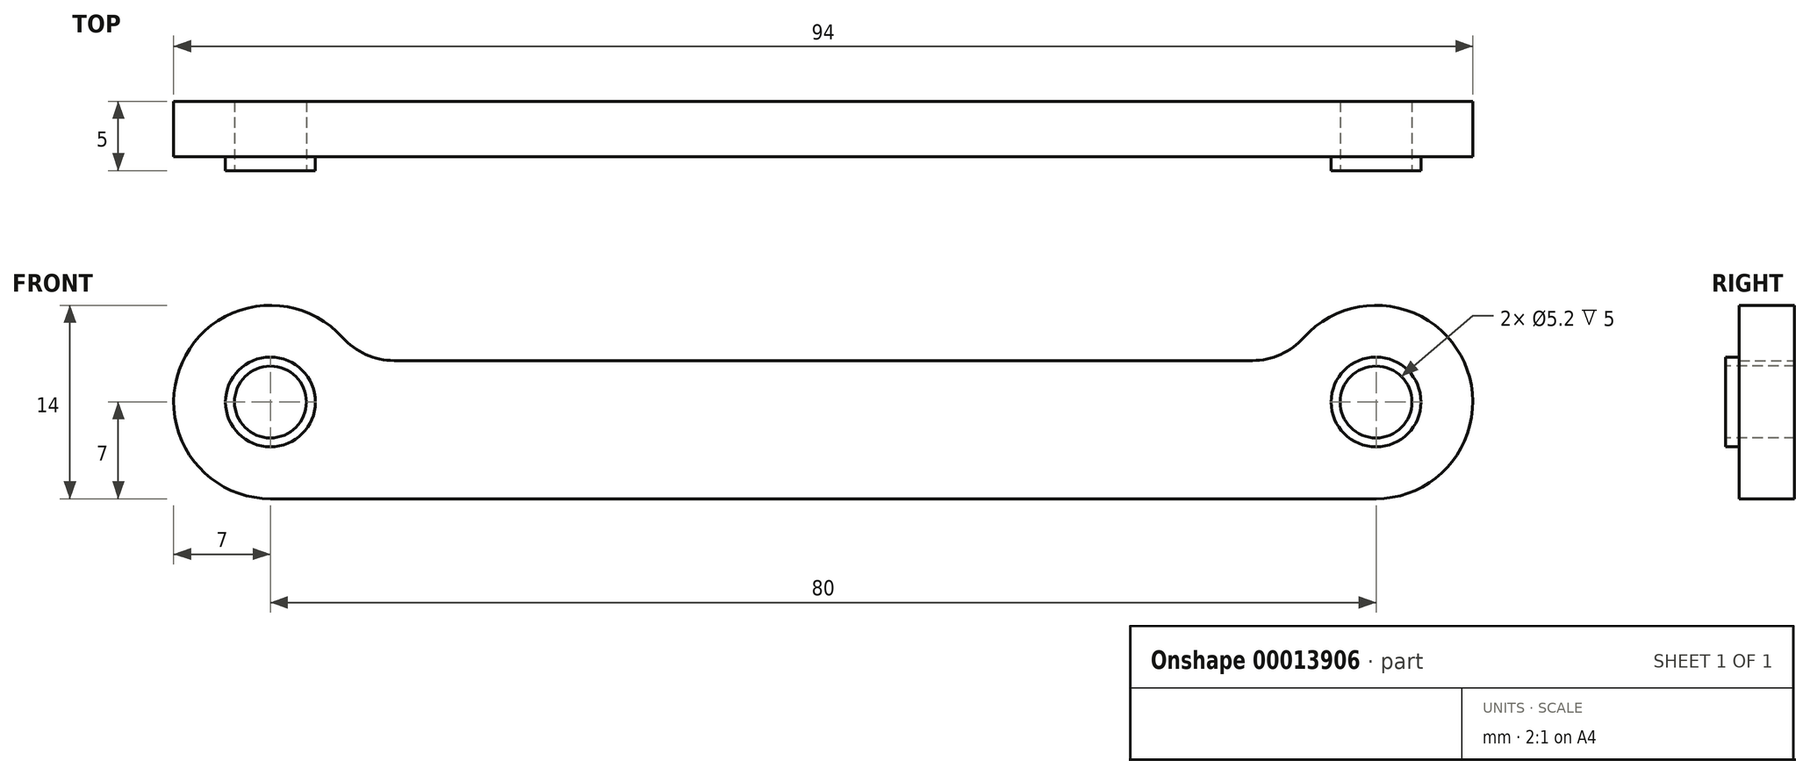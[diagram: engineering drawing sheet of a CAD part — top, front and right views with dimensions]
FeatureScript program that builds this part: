
annotation { "Feature Type Name" : "Feature", "Feature Type Description" : "" }
export const myFeature = defineFeature(function(context is Context, id is Id, definition is map)
    precondition{}
    {
        {
            var Q0;
            Q0=qCreatedBy(makeId("Front.planeOp"),FACE);
            var sketch = newSketch(context, id + "F0", { "sketchPlane" : qUnion([Q0])});
            skArc(sketch, "E0", {"start": v(-34.78, 11.67) * mm, "mid": v(-46.4, 9.86) * mm, "end": v(-40, 0) * mm});
            skArc(sketch, "E1", {"start": v(40, 0) * mm, "mid": v(46.4, 9.86) * mm, "end": v(34.78, 11.67) * mm});
            skLineSegment(sketch, "E2", {"start": v(-40, 0) * mm, "end": v(40, 0) * mm});
            skLineSegment(sketch, "E3", {"start": v(-31.06, 10) * mm, "end": v(31.06, 10) * mm});
            skCircle(sketch, "E4", {"center": v(0, 100) * mm, "radius": 100 * mm, "construction": true});
            skPoint(sketch, "E5.visualSharp", {"position": v(-33.68, 10) * mm});
            skArc(sketch, "E5.filletArc", {"start": v(-34.78, 11.67) * mm, "mid": v(-33.1, 10.44) * mm, "end": v(-31.06, 10) * mm});
            skPoint(sketch, "E6.visualSharp", {"position": v(33.68, 10) * mm});
            skArc(sketch, "E6.filletArc", {"start": v(31.06, 10) * mm, "mid": v(33.1, 10.44) * mm, "end": v(34.78, 11.67) * mm});
            skSolve(sketch);
        }
        {
            var Q0;
            Q0 = qSketchRegion(id + "F0", true);
            extrude(context, id + "F1", {"entities" : qUnion([Q0]), "depth" : 4 * mm});
        }
        {
            var Q0;
            Q0=makeQuery(id+"F1.opExtrude","CAP_FACE",FACE,{"disambiguationData":[OSD([sQuery(id+"F0.wireOp",EDGE,"E0"),sQuery(id+"F0.wireOp",EDGE,"E1"),sQuery(id+"F0.wireOp",EDGE,"E2"),sQuery(id+"F0.wireOp",EDGE,"E3"),sQuery(id+"F0.wireOp",EDGE,"E5.filletArc"),sQuery(id+"F0.wireOp",EDGE,"E6.filletArc")])],"isStart":false});
            var sketch = newSketch(context, id + "F2", { "sketchPlane" : qUnion([Q0])});
            skCircle(sketch, "E7", {"center": v(-40, 7) * mm, "radius": 3.25 * mm});
            skCircle(sketch, "E8", {"center": v(40, 7) * mm, "radius": 3.25 * mm});
            skSolve(sketch);
        }
        {
            var Q0;
            Q0 = qSketchRegion(id + "F2", true);
            extrude(context, id + "F3", {"entities" : qUnion([Q0]), "operationType" : NewBodyOperationType.ADD, "depth" : 1 * mm});
        }
        {
            var Q0;
            Q0=makeQuery(id+"F3.opExtrude","CAP_FACE",FACE,{"disambiguationData":[OSD([sQuery(id+"F2.wireOp",EDGE,"E7")])],"isStart":false});
            var sketch = newSketch(context, id + "F4", { "sketchPlane" : qUnion([Q0])});
            skCircle(sketch, "E9", {"center": v(-40, 7) * mm, "radius": 2.6 * mm});
            skCircle(sketch, "E10", {"center": v(40, 7) * mm, "radius": 2.6 * mm});
            skSolve(sketch);
        }
        {
            var Q0;
            Q0 = qSketchRegion(id + "F4", true);
            extrude(context, id + "F5", {"entities" : qUnion([Q0]), "operationType" : NewBodyOperationType.REMOVE, "endBound" : BoundingType.UP_TO_NEXT, "oppositeDirection" : true, "depth" : 25 * mm});
        }
    });
